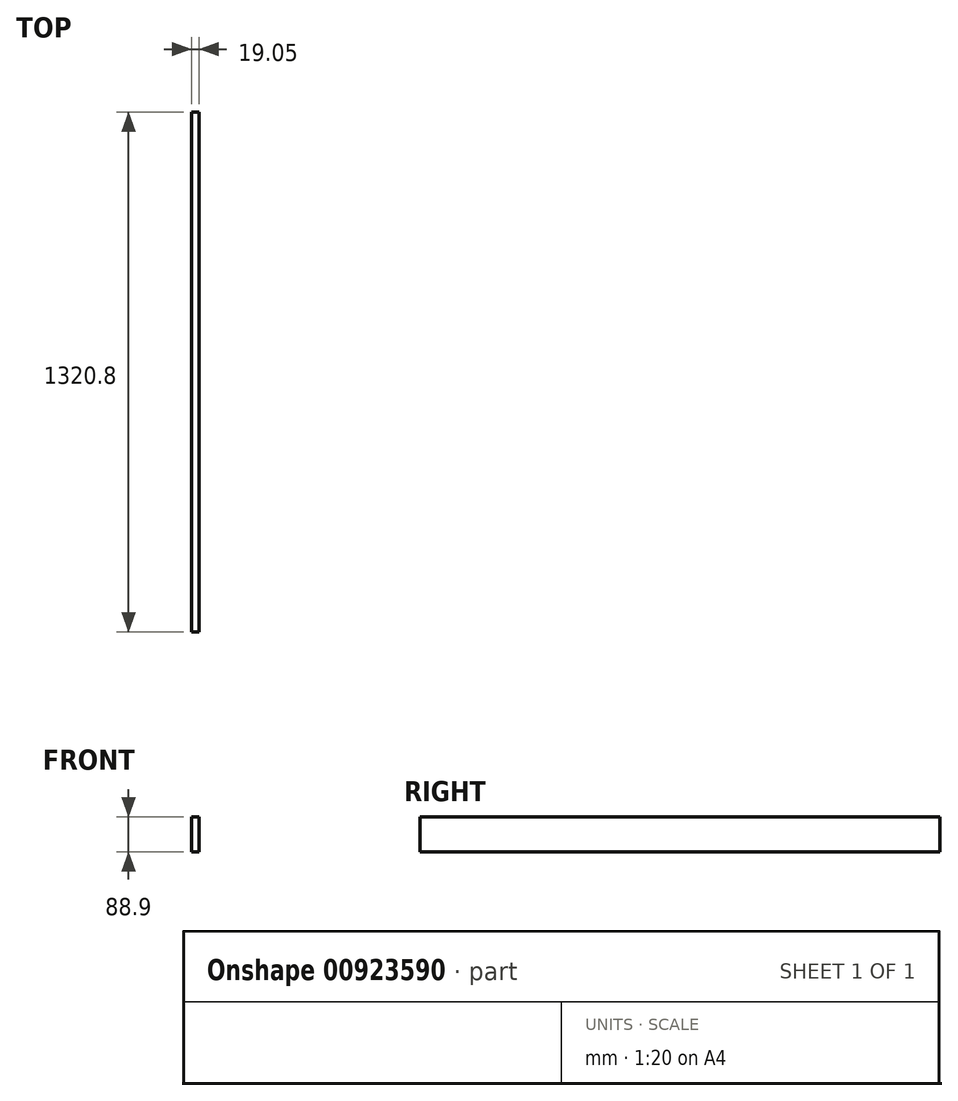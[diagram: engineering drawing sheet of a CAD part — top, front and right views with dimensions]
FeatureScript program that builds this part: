
annotation { "Feature Type Name" : "Feature", "Feature Type Description" : "" }
export const myFeature = defineFeature(function(context is Context, id is Id, definition is map)
    precondition{}
    {
        {
            var Q0;
            Q0=qCreatedBy(makeId("Right.planeOp"),FACE);
            var sketch = newSketch(context, id + "F0", { "sketchPlane" : qUnion([Q0])});
            skLineSegment(sketch, "E0.bottom", {"start": v(0, 0) * mm, "end": v(1320.8, 0) * mm});
            skLineSegment(sketch, "E0.top", {"start": v(0, 88.9) * mm, "end": v(1320.8, 88.9) * mm});
            skLineSegment(sketch, "E0.left", {"start": v(0, 0) * mm, "end": v(0, 88.9) * mm});
            skLineSegment(sketch, "E0.right", {"start": v(1320.8, 0) * mm, "end": v(1320.8, 88.9) * mm});
            skSolve(sketch);
        }
        {
            var Q0;
            Q0 = qSketchRegion(id + "F0", true);
            extrude(context, id + "F1", {"entities" : qUnion([Q0]), "depth" : 19.05 * mm, "offsetDistance" : 25.4 * mm});
        }
    });
